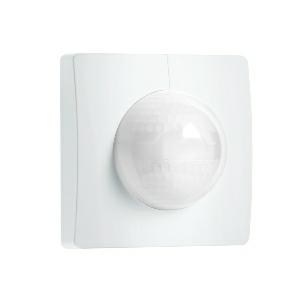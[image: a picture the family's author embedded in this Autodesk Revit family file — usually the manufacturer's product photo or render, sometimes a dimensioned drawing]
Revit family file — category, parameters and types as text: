
# Revit family: is_3180_058142
name_source: partatom
category: Elektroinstallationen
revit_build: Autodesk Revit 2016 (Build: 20190508_0715(x64)
units: mm (PartAtom-declared; Revit-internal decimal feet)

## family parameters
Basisbauteil = Fläche
Beim Laden mit Abzugskörper schneiden = Nein
Bemaßung runder Anschluss = Durchmesser verwenden
Beschriftungsausrichtung beibehalten = Nein
Gemeinsam genutzt = Nein
Raumberechnungspunkt = Nein
Teiletyp = Normal

## types (1)
- IS 3180
    Apparent Load = 0 VA
    Beschreibung = Type: Motion detectors; Dimensions (L x W x H): 78 x 94 x 94 mm; Sensor Technology: passive infrared; Application, place: Indoors; Application, room: corridor / aisle, function room / ancillary room, stairwell, multi-storey / underground car park, outdoors, all round the building, courtyard & driveway, Indoors; Installation site: wall, corner; Installation: Concealed wiring; Mounting height: 1,80 – 2,50 m; Optimum mounting height: 2 m; Detection angle: 180 °; Angle of aperture: 90 °; Sneak-by guard: Yes; Reach, radial: r = 4 m (25 m²); Reach, tangential: r = 20 m (628 m²); Twilight setting TEACH: Yes; Twilight setting: 2 – 1000 lx; Time setting: 0 sec – 1092 min; Constant-lighting control: Yes; Basic light level function: Yes; KNX functions: Photo-cell controller, Basic light level function, Light level, HVAC output, Constant-lighting control, Light output 2x, Presence output, Day / night function; With bus coupling: Yes; Settings via: ETS software, Remote control, Bus, Smart Remote; With remote control: No; Interconnection: Yes; IP-rating: IP20; Material: Plastic; Ambient temperature: -20 – 50 °C; Colour: white; Version: KNX - concealed, sq.; PU1, EAN: 4007841058142
    Height = 94 mm  [stored 0.308399 ft]
    Hersteller = Steinel
    Length = 78 mm  [stored 0.255906 ft]
    Maximum range = 22.153 m
    ModVariant = Nein
    Modell = 058142
    Mounting Type = Recessed
    Number of Poles = 1
    OnlyDefault = Ja
    Power Factor = 1
    Product Name = IS 3180
    Product group = Sensor-switched indoor light
    ProductGroupID = 30
    Protection Class = Protection class
    Protection Degree = IP 20
    RlxData = <blob elided: 167549 chars, md5=85646bf1>
    Sensor characteristics = Semi circular 145°-300°
    Sensor type = Passive (infrared)
    SensorDataFile = <blob elided: 5082 chars, md5=d953030a>
    Type of entry = Motion
    Typenbild = produkt1_058142.jpg
    Typenkommentare = Product without accessories
    URL = http://relux.com
    VarID = ---
    Voltage = 0 V
    Vorgabe-Ansicht = 1800 mm
    Weight = 0.00 kg
    Width = 94 mm  [stored 0.308399 ft]

note: [stored X ft] marks values corroborated as IEEE doubles in the binary element streams (Revit-internal decimal feet)

## geometry (parser evidence)
native form markers: Sweep x20
no freeform markers — native parametric forms only
